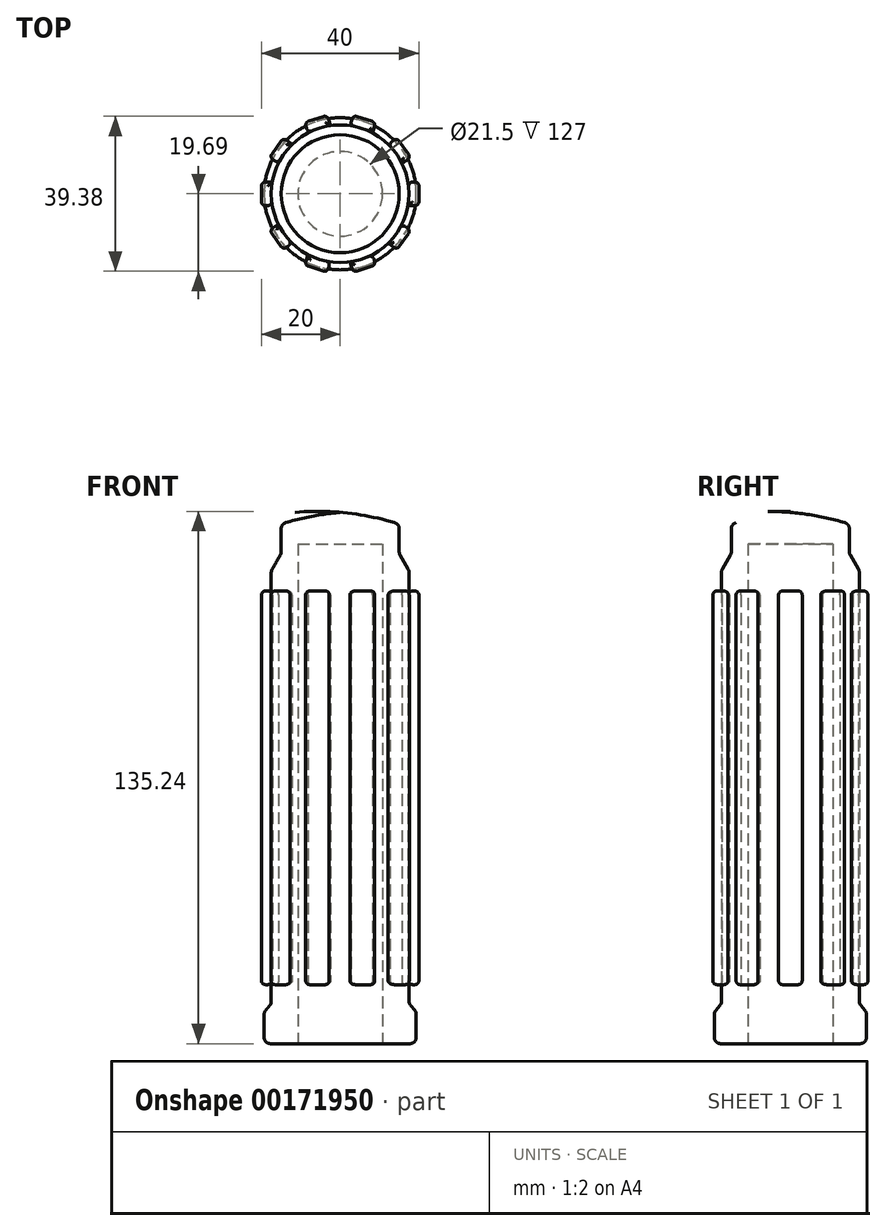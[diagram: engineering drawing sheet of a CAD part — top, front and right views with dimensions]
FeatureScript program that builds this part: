
annotation { "Feature Type Name" : "Feature", "Feature Type Description" : "" }
export const myFeature = defineFeature(function(context is Context, id is Id, definition is map)
    precondition{}
    {
        {
            var Q0;
            Q0=qCreatedBy(makeId("Front.planeOp"),FACE);
            var sketch = newSketch(context, id + "F0", { "sketchPlane" : qUnion([Q0])});
            skLineSegment(sketch, "E0", {"start": v(0, 0) * mm, "end": v(0, 155.81) * mm, "construction": true});
            skLineSegment(sketch, "E1", {"start": v(10.75, 0) * mm, "end": v(10.75, 127) * mm});
            skLineSegment(sketch, "E2", {"start": v(10.75, 127) * mm, "end": v(0, 127) * mm});
            skLineSegment(sketch, "E3", {"start": v(0, 127) * mm, "end": v(0, 135) * mm});
            skArc(sketch, "E4", {"start": v(15, 132) * mm, "mid": v(7.58, 133.93) * mm, "end": v(0, 135) * mm});
            skLineSegment(sketch, "E5", {"start": v(17.5, 10.17) * mm, "end": v(19.33, 8) * mm});
            skLineSegment(sketch, "E6", {"start": v(19.33, 8) * mm, "end": v(19.33, 0) * mm});
            skLineSegment(sketch, "E7", {"start": v(19.33, 0) * mm, "end": v(10.75, 0) * mm});
            skLineSegment(sketch, "E8", {"start": v(15, 132) * mm, "end": v(15, 124.5) * mm});
            skLineSegment(sketch, "E9", {"start": v(15, 124.5) * mm, "end": v(17.5, 120.17) * mm});
            skLineSegment(sketch, "E10", {"start": v(17.5, 120.17) * mm, "end": v(17.5, 10.17) * mm});
            skSolve(sketch);
        }
        {
            var Q0;
            Q0 = qSketchRegion(id + "F0", true);
            var Q1;
            Q1=sQuery(id+"F0.wireOp",EDGE,"E0");
            revolve(context, id + "F1", {"entities" : qUnion([Q0]), "axis" : qUnion([Q1]), "revolveType" : RevolveType.FULL});
        }
        {
            var Q0;
            Q0=makeQuery(id+"F1.opRevolve","SWEPT_EDGE",EDGE,{"disambiguationData":[OSD([sQuery(id+"F0.wireOp",EDGE,"E4"),sQuery(id+"F0.wireOp",EDGE,"E8")])]});
            var Q1;
            Q1=makeQuery(id+"F1.opRevolve","SWEPT_EDGE",EDGE,{"disambiguationData":[OSD([sQuery(id+"F0.wireOp",EDGE,"E9"),sQuery(id+"F0.wireOp",EDGE,"E10")])]});
            var Q2;
            Q2=makeQuery(id+"F1.opRevolve","SWEPT_EDGE",EDGE,{"disambiguationData":[OSD([sQuery(id+"F0.wireOp",EDGE,"E8"),sQuery(id+"F0.wireOp",EDGE,"E9")])]});
            var Q3;
            Q3=makeQuery(id+"F1.opRevolve","SWEPT_EDGE",EDGE,{"disambiguationData":[OSD([sQuery(id+"F0.wireOp",EDGE,"E5"),sQuery(id+"F0.wireOp",EDGE,"E10")])]});
            var Q4;
            Q4=makeQuery(id+"F1.opRevolve","SWEPT_EDGE",EDGE,{"disambiguationData":[OSD([sQuery(id+"F0.wireOp",EDGE,"E5"),sQuery(id+"F0.wireOp",EDGE,"E6")])]});
            var Q5;
            Q5=makeQuery(id+"F1.opRevolve","SWEPT_EDGE",EDGE,{"disambiguationData":[OSD([sQuery(id+"F0.wireOp",EDGE,"E6"),sQuery(id+"F0.wireOp",EDGE,"E7")])]});
            fillet(context, id + "F2", {"entities" : qUnion([Q0, Q1, Q2, Q3, Q4, Q5]), "radius" : 1.6 * mm, "tangentPropagation" : true, "allowEdgeOverflow" : false});
        }
        {
            var Q0;
            Q0=qCreatedBy(makeId("Right.planeOp"),FACE);
            cPlane(context, id + "F3", {"entities" : qUnion([Q0]), "cplaneType" : CPlaneType.OFFSET, "offset" : 20 * mm, "width" : 150 * mm, "height" : 150 * mm});
        }
        {
            var Q0;
            Q0=qCreatedBy(id+"F3.planeOp",FACE);
            var sketch = newSketch(context, id + "F4", { "sketchPlane" : qUnion([Q0])});
            skLineSegment(sketch, "E11.bottom", {"start": v(-3, 115) * mm, "end": v(3, 115) * mm});
            skLineSegment(sketch, "E11.top", {"start": v(-3, 15) * mm, "end": v(3, 15) * mm});
            skLineSegment(sketch, "E11.left", {"start": v(-3, 115) * mm, "end": v(-3, 15) * mm});
            skLineSegment(sketch, "E11.right", {"start": v(3, 115) * mm, "end": v(3, 15) * mm});
            skSolve(sketch);
        }
        {
            var Q0;
            Q0 = qSketchRegion(id + "F4", true);
            var Q1;
            Q1=makeQuery(id+"F1.opRevolve","SWEPT_FACE",FACE,{"disambiguationData":[OSD([sQuery(id+"F0.wireOp",EDGE,"E10")])]});
            extrude(context, id + "F5", {"entities" : qUnion([Q0]), "endBound" : BoundingType.UP_TO_SURFACE, "oppositeDirection" : true, "endBoundEntityFace" : qUnion([Q1]), "depth" : 25 * mm});
        }
        {
            var Q0;
            Q0=makeQuery(id+"F5.opExtrude","CAP_FACE",FACE,{"disambiguationData":[OSD([sQuery(id+"F4.wireOp",EDGE,"E11.bottom"),sQuery(id+"F4.wireOp",EDGE,"E11.top"),sQuery(id+"F4.wireOp",EDGE,"E11.left"),sQuery(id+"F4.wireOp",EDGE,"E11.right")])],"isStart":true});
            var Q1;
            Q1=makeQuery(id+"F5.opExtrude","CAP_EDGE",EDGE,{"disambiguationData":[OSD([sQuery(id+"F4.wireOp",EDGE,"E11.right")])],"isStart":false});
            var Q2;
            Q2=makeQuery(id+"F5.opExtrude","SWEPT_FACE",FACE,{"disambiguationData":[OSD([sQuery(id+"F4.wireOp",EDGE,"E11.bottom")])]});
            var Q3;
            Q3=makeQuery(id+"F5.opExtrude","SWEPT_FACE",FACE,{"disambiguationData":[OSD([sQuery(id+"F4.wireOp",EDGE,"E11.top")])]});
            fillet(context, id + "F6", {"entities" : qUnion([Q0, Q1, Q2, Q3]), "radius" : 1 * mm, "tangentPropagation" : true, "allowEdgeOverflow" : false});
        }
        {
            var Q0;
            Q0=makeQuery(id+"F5.opExtrude","SWEPT_BODY",BODY,{"disambiguationData":[OSD([sQuery(id+"F4.wireOp",EDGE,"E11.bottom"),sQuery(id+"F4.wireOp",EDGE,"E11.top"),sQuery(id+"F4.wireOp",EDGE,"E11.left"),sQuery(id+"F4.wireOp",EDGE,"E11.right")])]});
            var Q1;
            {var subQ0=sQuery(id+"F0.wireOp",EDGE,"E7");Q1=makeQuery(id+"F2.opFillet","BLEND_EDGE",EDGE,{"blendedFrom":[makeQuery(id+"F1.opRevolve","SWEPT_EDGE",EDGE,{"disambiguationData":[OSD([sQuery(id+"F0.wireOp",EDGE,"E6"),subQ0])]}),makeQuery(id+"F1.opRevolve","SWEPT_FACE",FACE,{"disambiguationData":[OSD([subQ0])]})],"blendedInto":[makeQuery(id+"F1.opRevolve","SWEPT_FACE",FACE,{"disambiguationData":[OSD([subQ0])]})]});}
            circularPattern(context, id + "F7", {"entities" : qUnion([Q0]), "axis" : qUnion([Q1]), "angle" : 360 * degree, "instanceCount" : 10, "equalSpace" : true});
        }
    });
